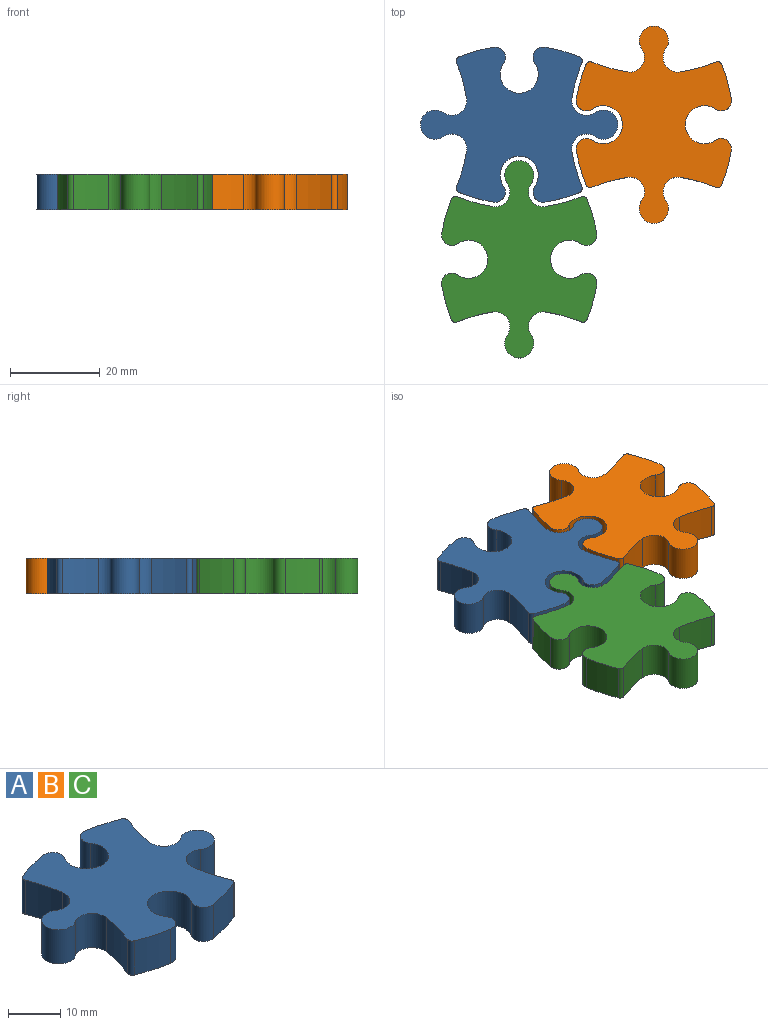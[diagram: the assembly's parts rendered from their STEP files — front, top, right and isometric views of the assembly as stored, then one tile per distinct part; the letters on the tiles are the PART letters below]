
ASSEMBLY  parts=3 mates=6
PART A: 26 faces, bbox 44x34.6x8 mm
  f0: plane 44x34.6mm, normal (0,0,-1), area 802.8mm2, adj f1,f2,f3,f4,f5,f6,f7,f8
  f1: cylinder r=2.3mm len=8mm, axis (0,0,1), area 43mm2, adj f0,f2,f20,f21
  f2: cylinder r=4.25mm len=8.5mm, axis (0,0,1), area 148.3mm2, adj f0,f1,f3,f21
  f3: cylinder r=2.3mm len=8mm, axis (0,0,1), area 43mm2, adj f0,f2,f4,f21
  f4: cylinder r=35.96mm len=8mm, axis (0,0,1), area 63.8mm2, adj f0,f3,f21,f22
  f5: cylinder r=36.96mm len=8mm, axis (0,0,1), area 66.1mm2, adj f0,f6,f21,f22
  f6: cylinder r=3.3mm len=8mm, axis (0,0,1), area 61.8mm2, adj f0,f5,f7,f21
  f7: cylinder r=3.25mm len=8mm, axis (0,0,1), area 113.4mm2, adj f0,f6,f8,f21
  f8: cylinder r=3.3mm len=8mm, axis (0,0,1), area 61.8mm2, adj f0,f7,f9,f21
  f9: cylinder r=36.96mm len=8mm, axis (0,0,1), area 66.1mm2, adj f0,f8,f21,f23
  f10: cylinder r=35.96mm len=8mm, axis (0,0,1), area 63.8mm2, adj f0,f11,f21,f23
  f11: cylinder r=2.3mm len=8mm, axis (0,0,1), area 43mm2, adj f0,f10,f12,f21
  f12: cylinder r=4.25mm len=8.5mm, axis (0,0,1), area 148.3mm2, adj f0,f11,f13,f21
  f13: cylinder r=2.3mm len=8mm, axis (0,0,1), area 43mm2, adj f0,f12,f14,f21
  f14: cylinder r=35.96mm len=8mm, axis (0,0,1), area 63.8mm2, adj f0,f13,f21,f24
  f15: cylinder r=36.96mm len=8mm, axis (0,0,1), area 66.1mm2, adj f0,f16,f21,f24
  f16: cylinder r=3.3mm len=8mm, axis (0,0,1), area 61.8mm2, adj f0,f15,f17,f21
  f17: cylinder r=3.25mm len=8mm, axis (0,0,1), area 113.4mm2, adj f0,f16,f18,f21
  f18: cylinder r=3.3mm len=8mm, axis (0,0,1), area 61.8mm2, adj f0,f17,f19,f21
  f19: cylinder r=36.96mm len=8mm, axis (0,0,1), area 66.1mm2, adj f0,f18,f21,f25
  f20: cylinder r=35.96mm len=8mm, axis (0,0,1), area 63.8mm2, adj f0,f1,f21,f25
  f21: plane 44x34.6mm, normal (0,0,1), area 802.8mm2, adj f1,f2,f3,f4,f5,f6,f7,f8
  f22: cylinder r=1mm len=8mm, axis (0,0,-1), area 12.6mm2, adj f0,f4,f5,f21
  f23: cylinder r=1mm len=8mm, axis (0,0,-1), area 12.6mm2, adj f0,f9,f10,f21
  f24: cylinder r=1mm len=8mm, axis (0,0,-1), area 12.6mm2, adj f0,f14,f15,f21
  f25: cylinder r=1mm len=8mm, axis (0,0,-1), area 12.6mm2, adj f0,f19,f20,f21
PART B: same geometry as A
PART C: same geometry as A
PLACE A t=(-4.7,0.96,0.51)mm fixed
PLACE B rot(axis=(0,0,-1),90deg) t=(25.3,0.96,0.51)mm
PLACE C rot(axis=(0,0,-1),90deg) t=(-4.7,-29.04,0.51)mm
MATE revolute B.f12 <-> A.f7  axis (0,0,1) through (14.05,0.96,8.51)mm
MATE revolute C.f17 <-> A.f12  axis (0,0,1) through (-4.7,-10.29,4.51)mm
MATE planar B.f21 <-> A.f21  axis (0,0,1) through (25.3,0.96,8.51)mm
MATE revolute A.f13 <-> C.f16  axis (0,0,1) through (-10.07,-14.04,8.51)mm
MATE planar C.f21 <-> A.f21  axis (0,0,1) through (-4.7,-29.04,8.51)mm
MATE revolute B.f11 <-> A.f8  axis (0,0,1) through (10.3,-4.41,8.51)mm
